# Revit family: Sanitary_Mirrors_Svedholm_Artemis
name_source: partatom
category: Furniture
revit_build: Autodesk Revit 2018 (Build: 20190510_1515(x64)
units: mm (PartAtom-declared; Revit-internal decimal feet)

## family parameters
Cut with Voids When Loaded = No
Host = Face
OmniClass Number = 23.21.37.13.15
OmniClass Title = Mirrors
Room Calculation Point = No
Shared = No

## types (1)
- ART - (103.200.002)
    BIMobject category = Mirrors
    Default Elevation = 1219 mm
    Description = An adjustable make-up mirror in high gloss chromium-plated steel with stainless steel wall fitting. Magnifying mirror alternatively plane mirror.
    Design country = Sweden
    Edition number = 1
    IFC Classification = Object
    Main material = Svedholm - Metal - Chrome
    Manufacturer = Svedholm
    Manufacturer country = Sweden
    Manufacturer name = Svedholm
    Masterformat 2014 Code = 08 83 00
    Masterformat 2014 Description = Mirrors
    Material main = Mirror Glass
    Material secondary = Chrome
    Mirror material = Svedholm - Glass - Mirror
    Model = Artemis
    NBS Reference Code = 71-55
    NBS Reference Description = Mirrors
    OmniClass Code = 23-21 37 13 15
    OmniClass Description = Mirrors
    Product Guid = ec0ef41a-ae4c-476e-a277-fa5ee7634d42
    Product SKU = Artemis
    Product data url = https://bimobject.com
    Product family = Artemis
    Product group = Mirrors
    Product name = Artemis
    Product url = https://www.svedholm.se
    QR code = https://bimobject.com
    Uniclass 1.4 Code = L8732
    Uniclass 1.4 Description = Mirrors
    Uniclass 2.0 Code = PR-71-55
    Uniclass 2.0 Description = Mirrors
    Uniclass 2015 Code = Pr_25_71_53
    Uniclass 2015 Name = Mirrors

## geometry (parser evidence)
native form markers: Sweep x2
no freeform markers — native parametric forms only
